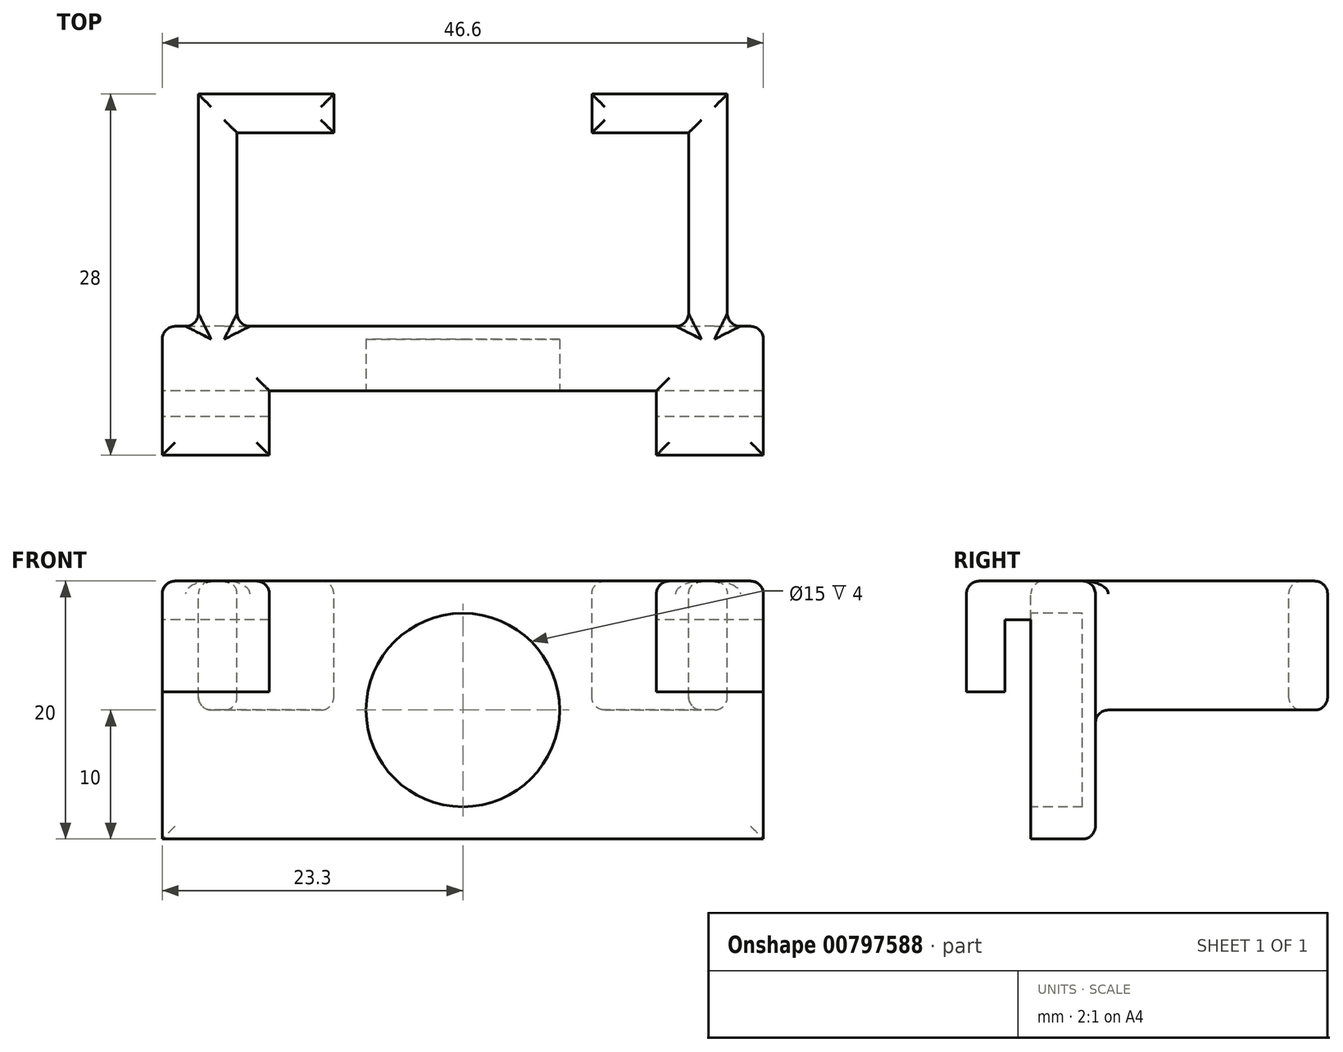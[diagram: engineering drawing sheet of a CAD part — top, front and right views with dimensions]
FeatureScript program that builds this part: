
annotation { "Feature Type Name" : "Feature", "Feature Type Description" : "" }
export const myFeature = defineFeature(function(context is Context, id is Id, definition is map)
    precondition{}
    {
        {
            var Q0;
            Q0=qCreatedBy(makeId("Right.planeOp"),FACE);
            var sketch = newSketch(context, id + "F0", { "sketchPlane" : qUnion([Q0])});
            skLineSegment(sketch, "E0", {"start": v(-5, 0) * mm, "end": v(0, 0) * mm});
            skLineSegment(sketch, "E1", {"start": v(0, 0) * mm, "end": v(0, 20) * mm});
            skLineSegment(sketch, "E2", {"start": v(0, 20) * mm, "end": v(-10, 20) * mm});
            skLineSegment(sketch, "E3", {"start": v(-10, 20) * mm, "end": v(-10, 11.4) * mm});
            skLineSegment(sketch, "E4", {"start": v(-10, 11.4) * mm, "end": v(-7, 11.4) * mm});
            skLineSegment(sketch, "E5", {"start": v(-7, 11.4) * mm, "end": v(-7, 17) * mm});
            skLineSegment(sketch, "E6", {"start": v(-7, 17) * mm, "end": v(-5, 17) * mm});
            skLineSegment(sketch, "E7", {"start": v(-5, 17) * mm, "end": v(-5, 0) * mm});
            skSolve(sketch);
        }
        {
            var Q0;
            Q0=makeQuery(id+"F0.imprint","IMPRINT",FACE,{"disambiguationData":[TD([[makeQuery(id+"F0.imprint","IMPRINT",EDGE,{"derivedFrom":sQuery(id+"F0.wireOp",EDGE,"E0")}),1.0]])]});
            extrude(context, id + "F1", {"entities" : qUnion([Q0]), "endBound" : BoundingType.SYMMETRIC, "depth" : 46.6 * mm, "offsetDistance" : 25 * mm});
        }
        {
            var Q0;
            Q0=makeQuery(id+"F1.opExtrude","SWEPT_FACE",FACE,{"disambiguationData":[OSD([sQuery(id+"F0.wireOp",EDGE,"E3")])]});
            var sketch = newSketch(context, id + "F2", { "sketchPlane" : qUnion([Q0])});
            skLineSegment(sketch, "E8.bottom", {"start": v(15, 11.4) * mm, "end": v(-15, 11.4) * mm});
            skLineSegment(sketch, "E8.top", {"start": v(15, 20) * mm, "end": v(-15, 20) * mm});
            skLineSegment(sketch, "E8.left", {"start": v(15, 11.4) * mm, "end": v(15, 20) * mm});
            skLineSegment(sketch, "E8.right", {"start": v(-15, 11.4) * mm, "end": v(-15, 20) * mm});
            skSolve(sketch);
        }
        {
            var Q0;
            Q0=makeQuery(id+"F2.imprint","IMPRINT",FACE,{"disambiguationData":[TD([[makeQuery(id+"F2.imprint","IMPRINT",EDGE,{"derivedFrom":sQuery(id+"F2.wireOp",EDGE,"E8.bottom")}),-1.0]])]});
            var Q1;
            Q1=makeQuery(id+"F1.opExtrude","SWEPT_FACE",FACE,{"disambiguationData":[OSD([sQuery(id+"F0.wireOp",EDGE,"E7")])]});
            extrude(context, id + "F3", {"entities" : qUnion([Q0]), "operationType" : NewBodyOperationType.REMOVE, "endBound" : BoundingType.UP_TO_SURFACE, "oppositeDirection" : true, "depth" : 25 * mm, "endBoundEntityFace" : qUnion([Q1]), "offsetDistance" : 25 * mm});
        }
        {
            var Q0;
            {var subQ0=sQuery(id+"F0.wireOp",EDGE,"E7");Q0=makeQuery(id+"F3.boolean.opBoolean","MERGE",FACE,{"derivedFrom":[makeQuery(id+"F1.opExtrude","SWEPT_FACE",FACE,{"disambiguationData":[OSD([subQ0])]}),makeQuery(id+"F3.opExtrude","CAP_FACE",FACE,{"disambiguationData":[OSD([subQ0])],"isStart":false})]});}
            var sketch = newSketch(context, id + "F4", { "sketchPlane" : qUnion([Q0])});
            skCircle(sketch, "E9", {"center": v(0, 10) * mm, "radius": 7.5 * mm});
            skLineSegment(sketch, "E10", {"start": v(0, 20) * mm, "end": v(0, 0) * mm, "construction": true});
            skSolve(sketch);
        }
        {
            var Q0;
            Q0=makeQuery(id+"F4.imprint","IMPRINT",FACE,{"disambiguationData":[TD([[makeQuery(id+"F4.imprint","IMPRINT",EDGE,{"derivedFrom":sQuery(id+"F4.wireOp",EDGE,"E9")}),1.0]])]});
            extrude(context, id + "F5", {"entities" : qUnion([Q0]), "operationType" : NewBodyOperationType.REMOVE, "oppositeDirection" : true, "depth" : 4 * mm, "offsetDistance" : 25 * mm});
        }
        {
            var Q0;
            Q0=makeQuery(id+"F1.opExtrude","SWEPT_FACE",FACE,{"disambiguationData":[OSD([sQuery(id+"F0.wireOp",EDGE,"E2")])]});
            var sketch = newSketch(context, id + "F6", { "sketchPlane" : qUnion([Q0])});
            skLineSegment(sketch, "E11", {"start": v(-20.5, 0) * mm, "end": v(-20.5, 18) * mm});
            skLineSegment(sketch, "E12", {"start": v(-20.5, 18) * mm, "end": v(-10, 18) * mm});
            skLineSegment(sketch, "E13", {"start": v(-10, 18) * mm, "end": v(-10, 15) * mm});
            skLineSegment(sketch, "E14", {"start": v(-10, 15) * mm, "end": v(-17.5, 15) * mm});
            skLineSegment(sketch, "E15", {"start": v(-17.5, 15) * mm, "end": v(-17.5, 0) * mm});
            skLineSegment(sketch, "E16", {"start": v(-17.5, 0) * mm, "end": v(-20.5, 0) * mm});
            skLineSegment(sketch, "E17.MirrorCS", {"start": v(10, 18) * mm, "end": v(10, 15) * mm});
            skLineSegment(sketch, "E18.MirrorCS", {"start": v(20.5, 18) * mm, "end": v(10, 18) * mm});
            skLineSegment(sketch, "E19.MirrorCS", {"start": v(20.5, 0) * mm, "end": v(20.5, 18) * mm});
            skLineSegment(sketch, "E20.MirrorCS", {"start": v(17.5, 15) * mm, "end": v(17.5, 0) * mm});
            skLineSegment(sketch, "E21.MirrorCS", {"start": v(17.5, 0) * mm, "end": v(20.5, 0) * mm});
            skLineSegment(sketch, "E22.MirrorCS", {"start": v(10, 15) * mm, "end": v(17.5, 15) * mm});
            skSolve(sketch);
        }
        {
            var Q0;
            Q0=makeQuery(id+"F6.imprint","IMPRINT",FACE,{"disambiguationData":[TD([[makeQuery(id+"F6.imprint","IMPRINT",EDGE,{"derivedFrom":sQuery(id+"F6.wireOp",EDGE,"E11")}),-1.0]])]});
            var Q1;
            Q1=makeQuery(id+"F6.imprint","IMPRINT",FACE,{"disambiguationData":[TD([[makeQuery(id+"F6.imprint","IMPRINT",EDGE,{"derivedFrom":sQuery(id+"F6.wireOp",EDGE,"E17.MirrorCS")}),1.0]])]});
            extrude(context, id + "F7", {"entities" : qUnion([Q0, Q1]), "operationType" : NewBodyOperationType.ADD, "oppositeDirection" : true, "depth" : 10 * mm, "offsetDistance" : 25 * mm});
        }
        {
            var Q0;
            Q0=makeQuery(id+"F7.boolean.opBoolean","MERGE",FACE,{"derivedFrom":[makeQuery(id+"F1.opExtrude","SWEPT_FACE",FACE,{"disambiguationData":[OSD([sQuery(id+"F0.wireOp",EDGE,"E2")])]}),makeQuery(id+"F7.opExtrude","CAP_FACE",FACE,{"disambiguationData":[OSD([sQuery(id+"F6.wireOp",EDGE,"E11"),sQuery(id+"F6.wireOp",EDGE,"E12"),sQuery(id+"F6.wireOp",EDGE,"E13"),sQuery(id+"F6.wireOp",EDGE,"E14"),sQuery(id+"F6.wireOp",EDGE,"E15"),sQuery(id+"F6.wireOp",EDGE,"E16")])],"isStart":true}),makeQuery(id+"F7.opExtrude","CAP_FACE",FACE,{"disambiguationData":[OSD([sQuery(id+"F6.wireOp",EDGE,"E17.MirrorCS"),sQuery(id+"F6.wireOp",EDGE,"E18.MirrorCS"),sQuery(id+"F6.wireOp",EDGE,"E19.MirrorCS"),sQuery(id+"F6.wireOp",EDGE,"E20.MirrorCS"),sQuery(id+"F6.wireOp",EDGE,"E21.MirrorCS"),sQuery(id+"F6.wireOp",EDGE,"E22.MirrorCS")])],"isStart":true})]});
            fillet(context, id + "F8", {"entities" : qUnion([Q0]), "radius" : 1 * mm, "tangentPropagation" : true, "allowEdgeOverflow" : false});
        }
        {
            var Q0;
            Q0=makeQuery(id+"F7.opExtrude","CAP_FACE",FACE,{"disambiguationData":[OSD([sQuery(id+"F6.wireOp",EDGE,"E17.MirrorCS"),sQuery(id+"F6.wireOp",EDGE,"E18.MirrorCS"),sQuery(id+"F6.wireOp",EDGE,"E19.MirrorCS"),sQuery(id+"F6.wireOp",EDGE,"E20.MirrorCS"),sQuery(id+"F6.wireOp",EDGE,"E21.MirrorCS"),sQuery(id+"F6.wireOp",EDGE,"E22.MirrorCS")])],"isStart":false});
            var Q1;
            Q1=makeQuery(id+"F7.opExtrude","CAP_FACE",FACE,{"disambiguationData":[OSD([sQuery(id+"F6.wireOp",EDGE,"E11"),sQuery(id+"F6.wireOp",EDGE,"E12"),sQuery(id+"F6.wireOp",EDGE,"E13"),sQuery(id+"F6.wireOp",EDGE,"E14"),sQuery(id+"F6.wireOp",EDGE,"E15"),sQuery(id+"F6.wireOp",EDGE,"E16")])],"isStart":false});
            var Q2;
            Q2=makeQuery(id+"F1.opExtrude","SWEPT_FACE",FACE,{"disambiguationData":[OSD([sQuery(id+"F0.wireOp",EDGE,"E1")])]});
            fillet(context, id + "F9", {"entities" : qUnion([Q0, Q1, Q2]), "radius" : 1 * mm, "tangentPropagation" : true, "allowEdgeOverflow" : false});
        }
    });
